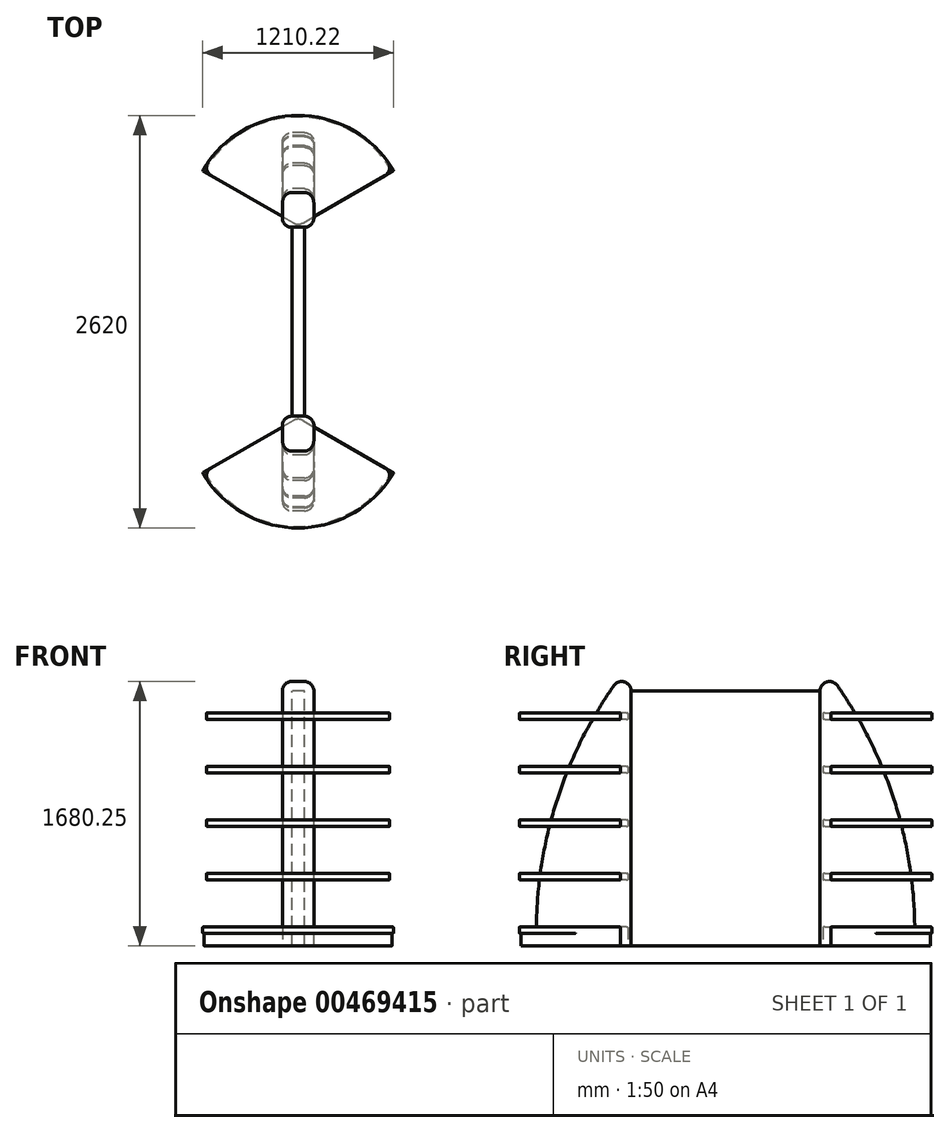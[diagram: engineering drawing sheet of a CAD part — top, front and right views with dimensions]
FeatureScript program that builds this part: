
annotation { "Feature Type Name" : "Feature", "Feature Type Description" : "" }
export const myFeature = defineFeature(function(context is Context, id is Id, definition is map)
    precondition{}
    {
        {
            assignVariable(context, id + "F0", {"name" : "x", "anyValue" : 600 * mm});
        }
        {
            assignVariable(context, id + "F1", {"name" : "z", "anyValue" : 200 * mm});
        }
        {
            assignVariable(context, id + "F2", {"name" : "F", "anyValue" : 3 * mm});
        }
        {
            var Q0;
            Q0=qCreatedBy(makeId("Right.planeOp"),FACE);
            var sketch = newSketch(context, id + "F3", { "sketchPlane" : qUnion([Q0])});
            skLineSegment(sketch, "E0", {"start": v(0, 0) * mm, "end": v(-600, 0) * mm});
            skLineSegment(sketch, "E1", {"start": v(0, 0) * mm, "end": v(0, 1800) * mm});
            skArc(sketch, "E2", {"start": v(0, 1800) * mm, "mid": v(-461.81, 953.94) * mm, "end": v(-600, 0) * mm});
            skSolve(sketch);
        }
        {
            var Q0;
            Q0 = qSketchRegion(id + "F3", true);
            extrude(context, id + "F4", {"entities" : qUnion([Q0]), "depth" : getVariable(context, 'z')});
        }
        {
            var Q0;
            Q0=makeQuery(id+"F4.opExtrude","CAP_FACE",FACE,{"disambiguationData":[OSD([sQuery(id+"F3.wireOp",EDGE,"E0"),sQuery(id+"F3.wireOp",EDGE,"E1"),sQuery(id+"F3.wireOp",EDGE,"M388cDUU-0T0g-FXCo-GjFR-7k1muveDL0A6")])],"isStart":false});
            cPlane(context, id + "F5", {"entities" : qUnion([Q0]), "cplaneType" : CPlaneType.OFFSET, "offset" : (getVariable(context, 'z')) / 2, "oppositeDirection" : true, "width" : 150 * mm, "height" : 150 * mm});
        }
        {
            var Q0;
            Q0=qCreatedBy(id+"F5.planeOp",FACE);
            var sketch = newSketch(context, id + "F6", { "sketchPlane" : qUnion([Q0])});
            skLineSegment(sketch, "E3.bottom", {"start": v(-10, 0) * mm, "end": v(-700, 0) * mm});
            skLineSegment(sketch, "E3.top", {"start": v(-10, 80) * mm, "end": v(-700, 80) * mm});
            skLineSegment(sketch, "E3.left", {"start": v(-10, 0) * mm, "end": v(-10, 80) * mm});
            skLineSegment(sketch, "E3.right", {"start": v(-700, 0) * mm, "end": v(-700, 80) * mm});
            skLineSegment(sketch, "E4.bottom", {"start": v(-10, 80) * mm, "end": v(-710, 80) * mm});
            skLineSegment(sketch, "E4.top", {"start": v(-10, 120) * mm, "end": v(-710, 120) * mm});
            skLineSegment(sketch, "E4.left", {"start": v(-10, 80) * mm, "end": v(-10, 120) * mm});
            skLineSegment(sketch, "E4.right", {"start": v(-710, 80) * mm, "end": v(-710, 120) * mm});
            skLineSegment(sketch, "E5.0.1.0", {"start": v(-10, 460) * mm, "end": v(-710, 460) * mm});
            skLineSegment(sketch, "E5.0.1.1", {"start": v(-10, 420) * mm, "end": v(-710, 420) * mm});
            skLineSegment(sketch, "E5.0.1.2", {"start": v(-710, 420) * mm, "end": v(-710, 460) * mm});
            skLineSegment(sketch, "E5.0.1.3", {"start": v(-10, 420) * mm, "end": v(-10, 460) * mm});
            skLineSegment(sketch, "E5.0.2.0", {"start": v(-10, 800) * mm, "end": v(-710, 800) * mm});
            skLineSegment(sketch, "E5.0.2.1", {"start": v(-10, 760) * mm, "end": v(-710, 760) * mm});
            skLineSegment(sketch, "E5.0.2.2", {"start": v(-710, 760) * mm, "end": v(-710, 800) * mm});
            skLineSegment(sketch, "E5.0.2.3", {"start": v(-10, 760) * mm, "end": v(-10, 800) * mm});
            skLineSegment(sketch, "E5.0.3.0", {"start": v(-10, 1140) * mm, "end": v(-710, 1140) * mm});
            skLineSegment(sketch, "E5.0.3.1", {"start": v(-10, 1100) * mm, "end": v(-710, 1100) * mm});
            skLineSegment(sketch, "E5.0.3.2", {"start": v(-710, 1100) * mm, "end": v(-710, 1140) * mm});
            skLineSegment(sketch, "E5.0.3.3", {"start": v(-10, 1100) * mm, "end": v(-10, 1140) * mm});
            skLineSegment(sketch, "E5.0.4.0", {"start": v(-10, 1480) * mm, "end": v(-710, 1480) * mm});
            skLineSegment(sketch, "E5.0.4.1", {"start": v(-10, 1440) * mm, "end": v(-710, 1440) * mm});
            skLineSegment(sketch, "E5.0.4.2", {"start": v(-710, 1440) * mm, "end": v(-710, 1480) * mm});
            skLineSegment(sketch, "E5.0.4.3", {"start": v(-10, 1440) * mm, "end": v(-10, 1480) * mm});
            skLineSegment(sketch, "E5.direction1", {"start": v(-710, 80) * mm, "end": v(-585, 80) * mm, "construction": true});
            skLineSegment(sketch, "E5.direction2", {"start": v(-710, 80) * mm, "end": v(-710, 420) * mm, "construction": true});
            skLineSegment(sketch, "E6", {"start": v(-10, 0) * mm, "end": v(0, 0) * mm, "construction": true});
            skSolve(sketch);
        }
        {
            var Q0;
            Q0 = qSketchRegion(id + "F6", true);
            var Q1;
            Q1=sQuery(id+"F6.wireOp",EDGE,"E3.left");
            revolve(context, id + "F7", {"entities" : qUnion([Q0]), "axis" : qUnion([Q1]), "revolveType" : RevolveType.SYMMETRIC, "angle" : 120 * degree});
        }
        {
            var Q0;
            Q0=makeQuery(id+"F7.opRevolve","CAP_EDGE",EDGE,{"disambiguationData":[OSD([sQuery(id+"F6.wireOp",EDGE,"E5.0.4.0")])],"isStart":false});
            var Q1;
            Q1=makeQuery(id+"F7.opRevolve","CAP_EDGE",EDGE,{"disambiguationData":[OSD([sQuery(id+"F6.wireOp",EDGE,"E5.0.4.0")])],"isStart":true});
            var Q2;
            Q2=makeQuery(id+"F7.opRevolve","SWEPT_FACE",FACE,{"disambiguationData":[OSD([sQuery(id+"F6.wireOp",EDGE,"E5.0.4.0")])]});
            var Q3;
            Q3=makeQuery(id+"F7.opRevolve","CAP_EDGE",EDGE,{"disambiguationData":[OSD([sQuery(id+"F6.wireOp",EDGE,"E5.0.3.0")])],"isStart":true});
            var Q4;
            Q4=makeQuery(id+"F7.opRevolve","SWEPT_EDGE",EDGE,{"disambiguationData":[OSD([sQuery(id+"F6.wireOp",EDGE,"E5.0.3.0"),sQuery(id+"F6.wireOp",EDGE,"E5.0.3.2")])]});
            var Q5;
            Q5=makeQuery(id+"F7.opRevolve","SWEPT_FACE",FACE,{"disambiguationData":[OSD([sQuery(id+"F6.wireOp",EDGE,"E5.0.2.0")])]});
            var Q6;
            Q6=makeQuery(id+"F7.opRevolve","CAP_EDGE",EDGE,{"disambiguationData":[OSD([sQuery(id+"F6.wireOp",EDGE,"E5.0.3.0")])],"isStart":false});
            var Q7;
            Q7=makeQuery(id+"F7.opRevolve","SWEPT_FACE",FACE,{"disambiguationData":[OSD([sQuery(id+"F6.wireOp",EDGE,"E5.0.1.0")])]});
            var Q8;
            Q8=makeQuery(id+"F7.opRevolve","SWEPT_FACE",FACE,{"disambiguationData":[OSD([sQuery(id+"F6.wireOp",EDGE,"E4.top")])]});
            var Q9;
            Q9=makeQuery(id+"F7.opRevolve","SWEPT_FACE",FACE,{"disambiguationData":[OSD([sQuery(id+"F6.wireOp",EDGE,"E5.0.4.1")])]});
            var Q10;
            Q10=makeQuery(id+"F7.opRevolve","SWEPT_FACE",FACE,{"disambiguationData":[OSD([sQuery(id+"F6.wireOp",EDGE,"E5.0.3.1")])]});
            var Q11;
            Q11=makeQuery(id+"F7.opRevolve","SWEPT_FACE",FACE,{"disambiguationData":[OSD([sQuery(id+"F6.wireOp",EDGE,"E5.0.2.1")])]});
            var Q12;
            Q12=makeQuery(id+"F7.opRevolve","SWEPT_FACE",FACE,{"disambiguationData":[OSD([sQuery(id+"F6.wireOp",EDGE,"E5.0.1.1")])]});
            var Q13;
            Q13=makeQuery(id+"F7.opRevolve","SWEPT_EDGE",EDGE,{"disambiguationData":[OSD([sQuery(id+"F6.wireOp",EDGE,"E4.bottom"),sQuery(id+"F6.wireOp",EDGE,"E4.right")])]});
            var Q14;
            Q14=makeQuery(id+"F7.opRevolve","CAP_EDGE",EDGE,{"disambiguationData":[OSD([sQuery(id+"F6.wireOp",EDGE,"E4.right")])],"isStart":true});
            var Q15;
            Q15=makeQuery(id+"F7.opRevolve","CAP_EDGE",EDGE,{"disambiguationData":[OSD([sQuery(id+"F6.wireOp",EDGE,"E3.right")])],"isStart":true});
            var Q16;
            Q16=makeQuery(id+"F7.opRevolve","CAP_EDGE",EDGE,{"disambiguationData":[OSD([sQuery(id+"F6.wireOp",EDGE,"E4.bottom")])],"isStart":true});
            var Q17;
            Q17=makeQuery(id+"F7.opRevolve","CAP_EDGE",EDGE,{"disambiguationData":[OSD([sQuery(id+"F6.wireOp",EDGE,"E3.right")])],"isStart":false});
            var Q18;
            Q18=makeQuery(id+"F7.opRevolve","CAP_EDGE",EDGE,{"disambiguationData":[OSD([sQuery(id+"F6.wireOp",EDGE,"E4.bottom")])],"isStart":false});
            var Q19;
            Q19=makeQuery(id+"F7.opRevolve","CAP_EDGE",EDGE,{"disambiguationData":[OSD([sQuery(id+"F6.wireOp",EDGE,"E4.right")])],"isStart":false});
            fillet(context, id + "F8", {"entities" : qUnion([Q0, Q1, Q2, Q3, Q4, Q5, Q6, Q7, Q8, Q9, Q10, Q11, Q12, Q13, Q14, Q15, Q16, Q17, Q18, Q19]), "radius" : getVariable(context, 'F'), "tangentPropagation" : true, "allowEdgeOverflow" : false});
        }
        {
            var Q0;
            Q0=makeQuery(id+"F4.opExtrude","SWEPT_EDGE",EDGE,{"disambiguationData":[OSD([sQuery(id+"F3.wireOp",EDGE,"E1"),sQuery(id+"F3.wireOp",EDGE,"E2")])]});
            var Q1;
            Q1=makeQuery(id+"F7.opRevolve","CAP_EDGE",EDGE,{"disambiguationData":[OSD([sQuery(id+"F6.wireOp",EDGE,"E5.0.4.2")])],"isStart":false});
            var Q2;
            Q2=makeQuery(id+"F7.opRevolve","CAP_EDGE",EDGE,{"disambiguationData":[OSD([sQuery(id+"F6.wireOp",EDGE,"E5.0.3.2")])],"isStart":false});
            var Q3;
            Q3=makeQuery(id+"F7.opRevolve","CAP_EDGE",EDGE,{"disambiguationData":[OSD([sQuery(id+"F6.wireOp",EDGE,"E5.0.2.2")])],"isStart":false});
            var Q4;
            Q4=makeQuery(id+"F7.opRevolve","CAP_EDGE",EDGE,{"disambiguationData":[OSD([sQuery(id+"F6.wireOp",EDGE,"E5.0.1.2")])],"isStart":false});
            var Q5;
            Q5=makeQuery(id+"F7.opRevolve","CAP_EDGE",EDGE,{"disambiguationData":[OSD([sQuery(id+"F6.wireOp",EDGE,"E5.0.1.2")])],"isStart":true});
            var Q6;
            Q6=makeQuery(id+"F7.opRevolve","CAP_EDGE",EDGE,{"disambiguationData":[OSD([sQuery(id+"F6.wireOp",EDGE,"E5.0.2.2")])],"isStart":true});
            var Q7;
            Q7=makeQuery(id+"F7.opRevolve","CAP_EDGE",EDGE,{"disambiguationData":[OSD([sQuery(id+"F6.wireOp",EDGE,"E5.0.3.2")])],"isStart":true});
            var Q8;
            Q8=makeQuery(id+"F7.opRevolve","CAP_EDGE",EDGE,{"disambiguationData":[OSD([sQuery(id+"F6.wireOp",EDGE,"E5.0.4.2")])],"isStart":true});
            var Q9;
            Q9=makeQuery(id+"F4.opExtrude","CAP_EDGE",EDGE,{"disambiguationData":[OSD([sQuery(id+"F3.wireOp",EDGE,"E2")])],"isStart":true});
            var Q10;
            Q10=makeQuery(id+"F4.opExtrude","CAP_EDGE",EDGE,{"disambiguationData":[OSD([sQuery(id+"F3.wireOp",EDGE,"E1")])],"isStart":true});
            var Q11;
            Q11=makeQuery(id+"F4.opExtrude","CAP_EDGE",EDGE,{"disambiguationData":[OSD([sQuery(id+"F3.wireOp",EDGE,"E2")])],"isStart":false});
            var Q12;
            Q12=makeQuery(id+"F4.opExtrude","CAP_EDGE",EDGE,{"disambiguationData":[OSD([sQuery(id+"F3.wireOp",EDGE,"E1")])],"isStart":false});
            var Q13;
            Q13=makeQuery(id+"F7.opRevolve","CAP_EDGE",EDGE,{"disambiguationData":[OSD([sQuery(id+"F6.wireOp",EDGE,"E5.0.4.3")])],"isStart":true});
            var Q14;
            Q14=makeQuery(id+"F7.opRevolve","CAP_EDGE",EDGE,{"disambiguationData":[OSD([sQuery(id+"F6.wireOp",EDGE,"E5.0.3.3")])],"isStart":true});
            var Q15;
            Q15=makeQuery(id+"F7.opRevolve","CAP_EDGE",EDGE,{"disambiguationData":[OSD([sQuery(id+"F6.wireOp",EDGE,"E5.0.2.3")])],"isStart":true});
            var Q16;
            Q16=makeQuery(id+"F7.opRevolve","CAP_EDGE",EDGE,{"disambiguationData":[OSD([sQuery(id+"F6.wireOp",EDGE,"E5.0.1.3")])],"isStart":true});
            var Q17;
            Q17=makeQuery(id+"F7.opRevolve","CAP_EDGE",EDGE,{"disambiguationData":[OSD([sQuery(id+"F6.wireOp",EDGE,"E3.left"),sQuery(id+"F6.wireOp",EDGE,"E4.left")])],"isStart":true});
            fillet(context, id + "F9", {"entities" : qUnion([Q0, Q1, Q2, Q3, Q4, Q5, Q6, Q7, Q8, Q9, Q10, Q11, Q12, Q13, Q14, Q15, Q16, Q17]), "radius" : (getVariable(context, 'F')) * 20, "tangentPropagation" : true, "allowEdgeOverflow" : false});
        }
        {
            var Q0;
            Q0=makeQuery(id+"F7.opRevolve","SWEPT_BODY",BODY,{"disambiguationData":[OSD([sQuery(id+"F6.wireOp",EDGE,"E3.bottom"),sQuery(id+"F6.wireOp",EDGE,"E3.left"),sQuery(id+"F6.wireOp",EDGE,"E3.right"),sQuery(id+"F6.wireOp",EDGE,"E4.bottom"),sQuery(id+"F6.wireOp",EDGE,"E4.top"),sQuery(id+"F6.wireOp",EDGE,"E4.left"),sQuery(id+"F6.wireOp",EDGE,"E4.right")])]});
            var Q1;
            Q1=makeQuery(id+"F7.opRevolve","SWEPT_BODY",BODY,{"disambiguationData":[OSD([sQuery(id+"F6.wireOp",EDGE,"E5.0.1.0"),sQuery(id+"F6.wireOp",EDGE,"E5.0.1.1"),sQuery(id+"F6.wireOp",EDGE,"E5.0.1.2"),sQuery(id+"F6.wireOp",EDGE,"E5.0.1.3")])]});
            var Q2;
            Q2=makeQuery(id+"F7.opRevolve","SWEPT_BODY",BODY,{"disambiguationData":[OSD([sQuery(id+"F6.wireOp",EDGE,"E5.0.2.0"),sQuery(id+"F6.wireOp",EDGE,"E5.0.2.1"),sQuery(id+"F6.wireOp",EDGE,"E5.0.2.2"),sQuery(id+"F6.wireOp",EDGE,"E5.0.2.3")])]});
            var Q3;
            Q3=makeQuery(id+"F7.opRevolve","SWEPT_BODY",BODY,{"disambiguationData":[OSD([sQuery(id+"F6.wireOp",EDGE,"E5.0.3.0"),sQuery(id+"F6.wireOp",EDGE,"E5.0.3.1"),sQuery(id+"F6.wireOp",EDGE,"E5.0.3.2"),sQuery(id+"F6.wireOp",EDGE,"E5.0.3.3")])]});
            var Q4;
            Q4=makeQuery(id+"F7.opRevolve","SWEPT_BODY",BODY,{"disambiguationData":[OSD([sQuery(id+"F6.wireOp",EDGE,"E5.0.4.0"),sQuery(id+"F6.wireOp",EDGE,"E5.0.4.1"),sQuery(id+"F6.wireOp",EDGE,"E5.0.4.2"),sQuery(id+"F6.wireOp",EDGE,"E5.0.4.3")])]});
            var Q5;
            Q5=makeQuery(id+"F4.opExtrude","SWEPT_BODY",BODY,{"disambiguationData":[OSD([sQuery(id+"F3.wireOp",EDGE,"E0"),sQuery(id+"F3.wireOp",EDGE,"E1"),sQuery(id+"F3.wireOp",EDGE,"E2")])]});
            booleanBodies(context, id + "F10", {"operationType" : BooleanOperationType.SUBTRACTION, "tools" : qUnion([Q0, Q1, Q2, Q3, Q4]), "targets" : qUnion([Q5]), "keepTools" : true});
        }
        {
            var Q0;
            Q0=makeQuery(id+"F4.opExtrude","SWEPT_FACE",FACE,{"disambiguationData":[OSD([sQuery(id+"F3.wireOp",EDGE,"E1")])]});
            extrude(context, id + "F11", {"entities" : qUnion([Q0]), "depth" : (getVariable(context, 'x')) * 2});
        }
        {
            var Q0;
            Q0=makeQuery(id+"F11.opExtrude","CAP_FACE",FACE,{"disambiguationData":[OSD([sQuery(id+"F3.wireOp",EDGE,"E1")])],"isStart":false});
            cPlane(context, id + "F12", {"entities" : qUnion([Q0]), "cplaneType" : CPlaneType.OFFSET, "offset" : getVariable(context, 'x'), "oppositeDirection" : true, "width" : 150 * mm, "height" : 150 * mm});
        }
        {
            var Q0;
            Q0=makeQuery(id+"F7.opRevolve","SWEPT_BODY",BODY,{"disambiguationData":[OSD([sQuery(id+"F6.wireOp",EDGE,"E5.0.4.0"),sQuery(id+"F6.wireOp",EDGE,"E5.0.4.1"),sQuery(id+"F6.wireOp",EDGE,"E5.0.4.2"),sQuery(id+"F6.wireOp",EDGE,"E5.0.4.3")])]});
            var Q1;
            Q1=makeQuery(id+"F4.opExtrude","SWEPT_BODY",BODY,{"disambiguationData":[OSD([sQuery(id+"F3.wireOp",EDGE,"E0"),sQuery(id+"F3.wireOp",EDGE,"E1"),sQuery(id+"F3.wireOp",EDGE,"E2")])]});
            var Q2;
            Q2=makeQuery(id+"F7.opRevolve","SWEPT_BODY",BODY,{"disambiguationData":[OSD([sQuery(id+"F6.wireOp",EDGE,"E3.bottom"),sQuery(id+"F6.wireOp",EDGE,"E3.left"),sQuery(id+"F6.wireOp",EDGE,"E3.right"),sQuery(id+"F6.wireOp",EDGE,"E4.bottom"),sQuery(id+"F6.wireOp",EDGE,"E4.top"),sQuery(id+"F6.wireOp",EDGE,"E4.left"),sQuery(id+"F6.wireOp",EDGE,"E4.right")])]});
            var Q3;
            Q3=makeQuery(id+"F7.opRevolve","SWEPT_BODY",BODY,{"disambiguationData":[OSD([sQuery(id+"F6.wireOp",EDGE,"E5.0.1.0"),sQuery(id+"F6.wireOp",EDGE,"E5.0.1.1"),sQuery(id+"F6.wireOp",EDGE,"E5.0.1.2"),sQuery(id+"F6.wireOp",EDGE,"E5.0.1.3")])]});
            var Q4;
            Q4=makeQuery(id+"F7.opRevolve","SWEPT_BODY",BODY,{"disambiguationData":[OSD([sQuery(id+"F6.wireOp",EDGE,"E5.0.2.0"),sQuery(id+"F6.wireOp",EDGE,"E5.0.2.1"),sQuery(id+"F6.wireOp",EDGE,"E5.0.2.2"),sQuery(id+"F6.wireOp",EDGE,"E5.0.2.3")])]});
            var Q5;
            Q5=makeQuery(id+"F7.opRevolve","SWEPT_BODY",BODY,{"disambiguationData":[OSD([sQuery(id+"F6.wireOp",EDGE,"E5.0.3.0"),sQuery(id+"F6.wireOp",EDGE,"E5.0.3.1"),sQuery(id+"F6.wireOp",EDGE,"E5.0.3.2"),sQuery(id+"F6.wireOp",EDGE,"E5.0.3.3")])]});
            var Q6;
            Q6=qCreatedBy(id+"F12.planeOp",FACE);
            mirror(context, id + "F13", {"entities" : qUnion([Q0, Q1, Q2, Q3, Q4, Q5]), "mirrorPlane" : qUnion([Q6])});
        }
    });
